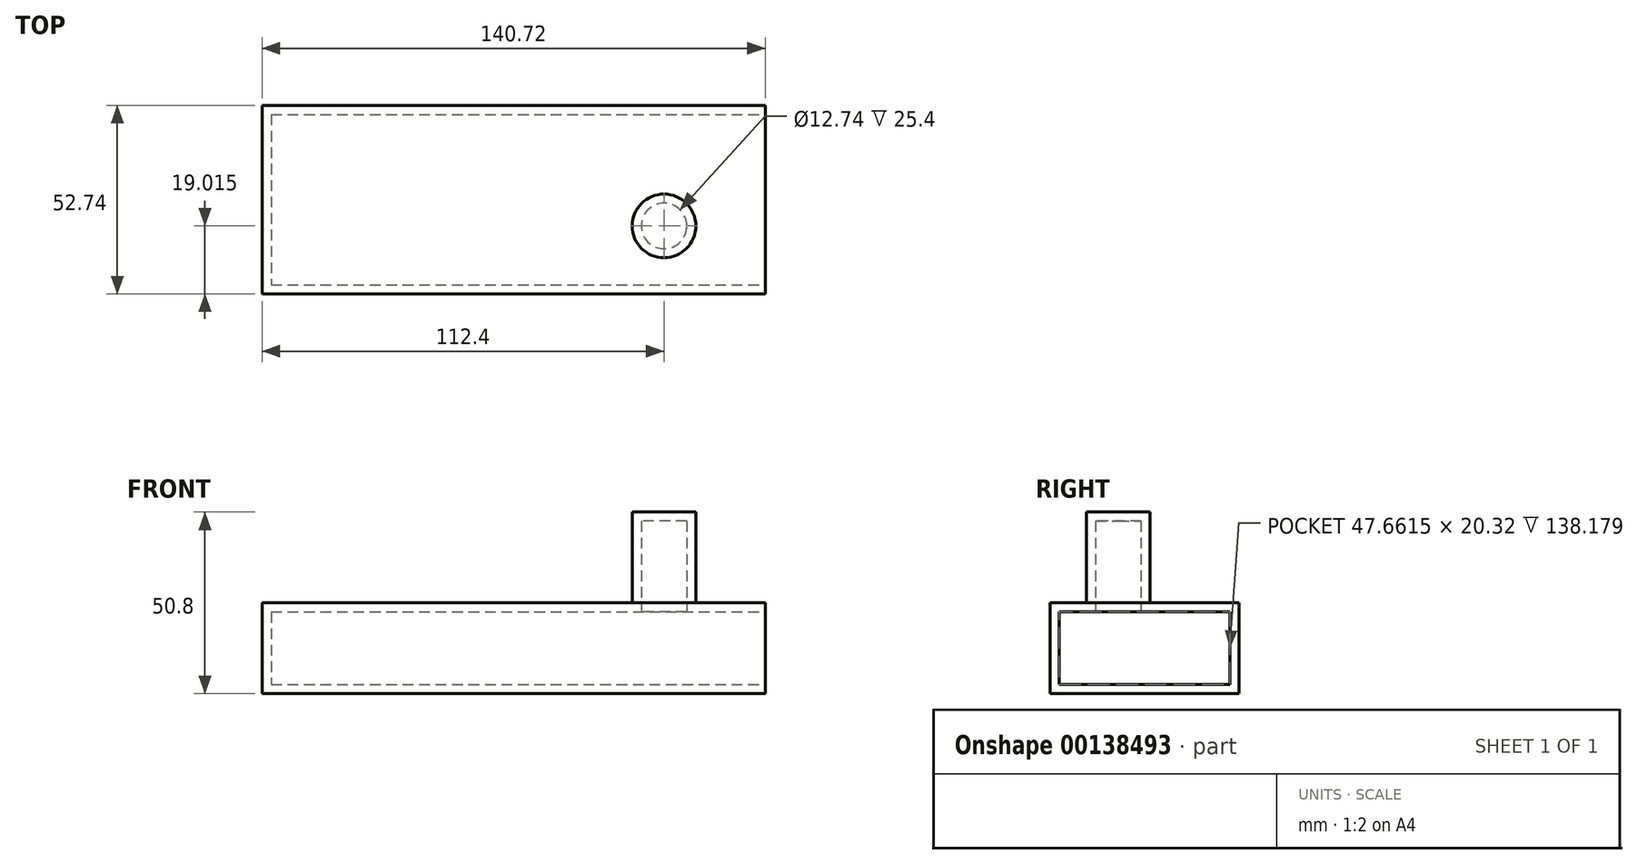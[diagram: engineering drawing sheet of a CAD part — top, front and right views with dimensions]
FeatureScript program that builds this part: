
annotation { "Feature Type Name" : "Feature", "Feature Type Description" : "" }
export const myFeature = defineFeature(function(context is Context, id is Id, definition is map)
    precondition{}
    {
        {
            var Q0;
            Q0=qCreatedBy(makeId("Top.planeOp"),FACE);
            var sketch = newSketch(context, id + "F0", { "sketchPlane" : qUnion([Q0])});
            skLineSegment(sketch, "E0.bottom", {"start": v(-69.18, 28.84) * mm, "end": v(71.54, 28.84) * mm});
            skLineSegment(sketch, "E0.top", {"start": v(-69.18, -23.9) * mm, "end": v(71.54, -23.9) * mm});
            skLineSegment(sketch, "E0.left", {"start": v(-69.18, 28.84) * mm, "end": v(-69.18, -23.9) * mm});
            skLineSegment(sketch, "E0.right", {"start": v(71.54, 28.84) * mm, "end": v(71.54, -23.9) * mm});
            skSolve(sketch);
        }
        {
            var Q0;
            Q0 = qSketchRegion(id + "F0", true);
            extrude(context, id + "F1", {"entities" : qUnion([Q0]), "depth" : 25.4 * mm});
        }
        {
            var Q0;
            Q0=makeQuery(id+"F1.opExtrude","CAP_FACE",FACE,{"disambiguationData":[OSD([sQuery(id+"F0.wireOp",EDGE,"E0.bottom"),sQuery(id+"F0.wireOp",EDGE,"E0.top"),sQuery(id+"F0.wireOp",EDGE,"E0.left"),sQuery(id+"F0.wireOp",EDGE,"E0.right")])],"isStart":false});
            var sketch = newSketch(context, id + "F2", { "sketchPlane" : qUnion([Q0])});
            skCircle(sketch, "E1", {"center": v(43.22, -4.89) * mm, "radius": 8.91 * mm});
            skSolve(sketch);
        }
        {
            var Q0;
            Q0 = qSketchRegion(id + "F2", true);
            extrude(context, id + "F3", {"entities" : qUnion([Q0]), "operationType" : NewBodyOperationType.ADD, "depth" : 25.4 * mm});
        }
        {
            var Q0;
            Q0=makeQuery(id+"F1.opExtrude","SWEPT_FACE",FACE,{"disambiguationData":[OSD([sQuery(id+"F0.wireOp",EDGE,"E0.right")])]});
            shell(context, id + "F4", {"entities" : qUnion([Q0]), "thickness" : 2.54 * mm});
        }
    });
